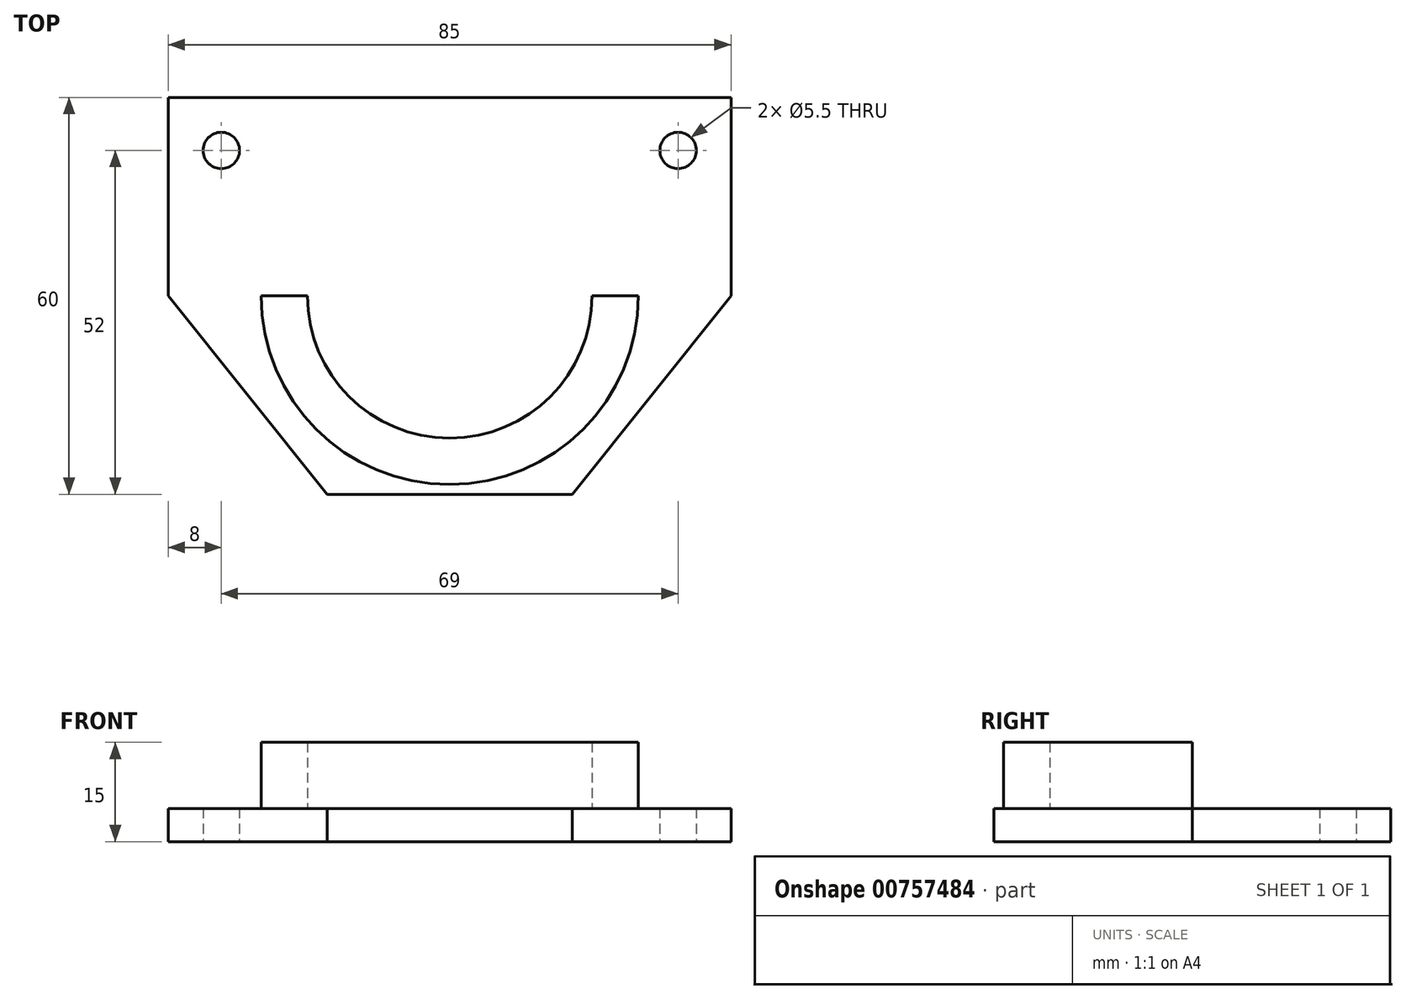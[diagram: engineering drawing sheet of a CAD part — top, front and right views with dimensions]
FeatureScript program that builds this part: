
annotation { "Feature Type Name" : "Feature", "Feature Type Description" : "" }
export const myFeature = defineFeature(function(context is Context, id is Id, definition is map)
    precondition{}
    {
        {
            var Q0;
            Q0=qCreatedBy(makeId("Top.planeOp"),FACE);
            var sketch = newSketch(context, id + "F0", { "sketchPlane" : qUnion([Q0])});
            skLineSegment(sketch, "E0.bottom", {"start": v(-42.5, 30) * mm, "end": v(42.5, 30) * mm});
            skLineSegment(sketch, "E0.top", {"start": v(-18.5, -30) * mm, "end": v(18.5, -30) * mm});
            skLineSegment(sketch, "E0.left", {"start": v(-42.5, 30) * mm, "end": v(-42.5, 0) * mm});
            skLineSegment(sketch, "E0.right", {"start": v(42.5, 30) * mm, "end": v(42.5, 0) * mm});
            skPoint(sketch, "E0.middle", {"position": v(0, 0) * mm});
            skLineSegment(sketch, "E1", {"start": v(-42.5, 0) * mm, "end": v(-18.5, -30) * mm});
            skLineSegment(sketch, "E2", {"start": v(42.5, 0) * mm, "end": v(18.5, -30) * mm});
            skPoint(sketch, "E3.orphan", {"position": v(-42.5, -30) * mm});
            skPoint(sketch, "E4.orphan", {"position": v(42.5, -30) * mm});
            skPoint(sketch, "E5", {"position": v(-34.5, 22) * mm});
            skPoint(sketch, "E6", {"position": v(34.5, 22) * mm});
            skSolve(sketch);
        }
        {
            var Q0;
            Q0=makeQuery(id+"F0.imprint","IMPRINT",FACE,{"disambiguationData":[TD([[makeQuery(id+"F0.imprint","IMPRINT",EDGE,{"derivedFrom":sQuery(id+"F0.wireOp",EDGE,"E0.bottom")}),-1.0]])]});
            extrude(context, id + "F1", {"entities" : qUnion([Q0]), "depth" : 5 * mm, "offsetDistance" : 25 * mm});
        }
        {
            var Q0;
            Q0=qCreatedBy(makeId("Top.planeOp"),FACE);
            var sketch = newSketch(context, id + "F2", { "sketchPlane" : qUnion([Q0])});
            skArc(sketch, "E7", {"start": v(-21.5, 0) * mm, "mid": v(0, -21.5) * mm, "end": v(21.5, 0) * mm});
            skArc(sketch, "E8", {"start": v(-28.5, 0) * mm, "mid": v(0, -28.5) * mm, "end": v(28.5, 0) * mm});
            skLineSegment(sketch, "E9", {"start": v(-28.5, 0) * mm, "end": v(-21.5, 0) * mm});
            skLineSegment(sketch, "E10", {"start": v(21.5, 0) * mm, "end": v(28.5, 0) * mm});
            skSolve(sketch);
        }
        {
            var Q0;
            Q0 = qSketchRegion(id + "F2", true);
            extrude(context, id + "F3", {"entities" : qUnion([Q0]), "operationType" : NewBodyOperationType.ADD, "depth" : 15 * mm, "offsetDistance" : 25 * mm});
        }
        {
            var Q0;
            Q0=sQuery(id+"F0.wireOp",VERTEX,"E5");
            var Q1;
            Q1=sQuery(id+"F0.wireOp",VERTEX,"E6");
            var Q2;
            Q2=makeQuery(id+"F1.opExtrude","SWEPT_BODY",BODY,{"disambiguationData":[OSD([sQuery(id+"F0.wireOp",EDGE,"E0.bottom"),sQuery(id+"F0.wireOp",EDGE,"E0.top"),sQuery(id+"F0.wireOp",EDGE,"E0.left"),sQuery(id+"F0.wireOp",EDGE,"E0.right"),sQuery(id+"F0.wireOp",EDGE,"E1"),sQuery(id+"F0.wireOp",EDGE,"E2")])]});
            hole(context, id + "F4", {"style" : HoleStyle.SIMPLE, "endStyle" : HoleEndStyle.BLIND, "oppositeDirection" : true, "standardTappedOrClearance" : lookupTablePath({ "standard" : "ISO", "fit" : "Normal", "size" : "M5", "type" : "Clearance" }), "standardBlindInLast" : lookupTablePath({ "fit" : "Standard", "standard" : "ISO", "size" : "M5", "type" : "Clearance" }), "holeDiameter" : 5.5 * mm, "majorDiameter" : 5 * mm, "holeDepth" : 13.5 * mm, "isTappedThrough" : true, "tappedDepth" : 12 * mm, "tapClearance" : 3, "locations" : qUnion([Q0, Q1]), "scope" : qUnion([Q2])});
        }
    });
